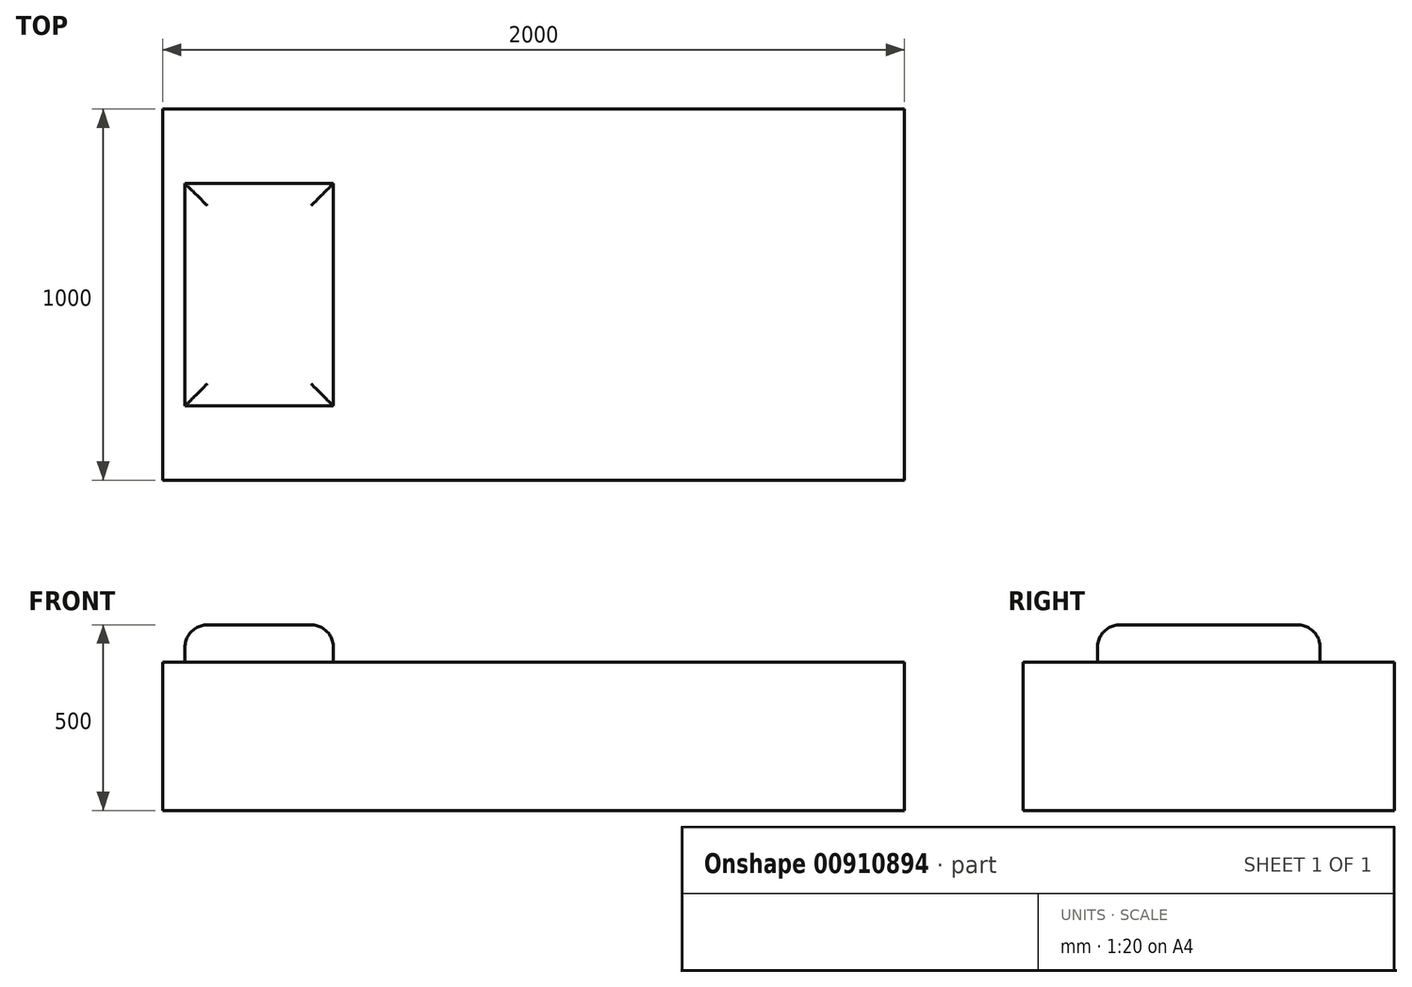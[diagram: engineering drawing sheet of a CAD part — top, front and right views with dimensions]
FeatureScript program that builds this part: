
annotation { "Feature Type Name" : "Feature", "Feature Type Description" : "" }
export const myFeature = defineFeature(function(context is Context, id is Id, definition is map)
    precondition{}
    {
        {
            var Q0;
            Q0=qCreatedBy(makeId("Top.planeOp"),FACE);
            var sketch = newSketch(context, id + "F0", { "sketchPlane" : qUnion([Q0])});
            skLineSegment(sketch, "E0.bottom", {"start": v(-998.68, 245.15) * mm, "end": v(1001.32, 245.15) * mm});
            skLineSegment(sketch, "E0.top", {"start": v(-998.68, -754.85) * mm, "end": v(1001.32, -754.85) * mm});
            skLineSegment(sketch, "E0.left", {"start": v(-998.68, 245.15) * mm, "end": v(-998.68, -754.85) * mm});
            skLineSegment(sketch, "E0.right", {"start": v(1001.32, 245.15) * mm, "end": v(1001.32, -754.85) * mm});
            skSolve(sketch);
        }
        {
            var Q0;
            Q0=makeQuery(id+"F0.imprint","IMPRINT",FACE,{"disambiguationData":[TD([[makeQuery(id+"F0.imprint","IMPRINT",EDGE,{"derivedFrom":sQuery(id+"F0.wireOp",EDGE,"E0.bottom")}),-1.0]])]});
            var sketch = newSketch(context, id + "F1", { "sketchPlane" : qUnion([Q0])});
            skLineSegment(sketch, "E1.bottom", {"start": v(-538.09, -554.85) * mm, "end": v(-938.09, -554.85) * mm});
            skLineSegment(sketch, "E1.top", {"start": v(-538.09, 45.15) * mm, "end": v(-938.09, 45.15) * mm});
            skLineSegment(sketch, "E1.left", {"start": v(-538.09, -554.85) * mm, "end": v(-538.09, 45.15) * mm});
            skLineSegment(sketch, "E1.right", {"start": v(-938.09, -554.85) * mm, "end": v(-938.09, 45.15) * mm});
            skSolve(sketch);
        }
        {
            var Q0;
            Q0=makeQuery(id+"F0.imprint","IMPRINT",FACE,{"disambiguationData":[TD([[makeQuery(id+"F0.imprint","IMPRINT",EDGE,{"derivedFrom":sQuery(id+"F0.wireOp",EDGE,"E0.bottom")}),-1.0]])]});
            extrude(context, id + "F2", {"entities" : qUnion([Q0]), "oppositeDirection" : true, "depth" : 400 * mm, "offsetDistance" : 25 * mm});
        }
        {
            var Q0;
            Q0=makeQuery(id+"F1.imprint","IMPRINT",FACE,{"disambiguationData":[TD([[makeQuery(id+"F1.imprint","IMPRINT",EDGE,{"derivedFrom":sQuery(id+"F1.wireOp",EDGE,"E1.bottom")}),-1.0]])]});
            extrude(context, id + "F3", {"entities" : qUnion([Q0]), "operationType" : NewBodyOperationType.ADD, "depth" : 100 * mm, "offsetDistance" : 25 * mm});
        }
        {
            var Q0;
            Q0=makeQuery(id+"F3.opExtrude","CAP_EDGE",EDGE,{"disambiguationData":[OSD([sQuery(id+"F1.wireOp",EDGE,"E1.bottom")])],"isStart":false});
            var Q1;
            Q1=makeQuery(id+"F3.opExtrude","CAP_EDGE",EDGE,{"disambiguationData":[OSD([sQuery(id+"F1.wireOp",EDGE,"E1.top")])],"isStart":false});
            var Q2;
            Q2=makeQuery(id+"F3.opExtrude","CAP_EDGE",EDGE,{"disambiguationData":[OSD([sQuery(id+"F1.wireOp",EDGE,"E1.left")])],"isStart":false});
            var Q3;
            Q3=makeQuery(id+"F3.opExtrude","CAP_EDGE",EDGE,{"disambiguationData":[OSD([sQuery(id+"F1.wireOp",EDGE,"E1.right")])],"isStart":false});
            fillet(context, id + "F4", {"entities" : qUnion([Q0, Q1, Q2, Q3]), "radius" : 60 * mm, "tangentPropagation" : true, "allowEdgeOverflow" : false});
        }
    });
